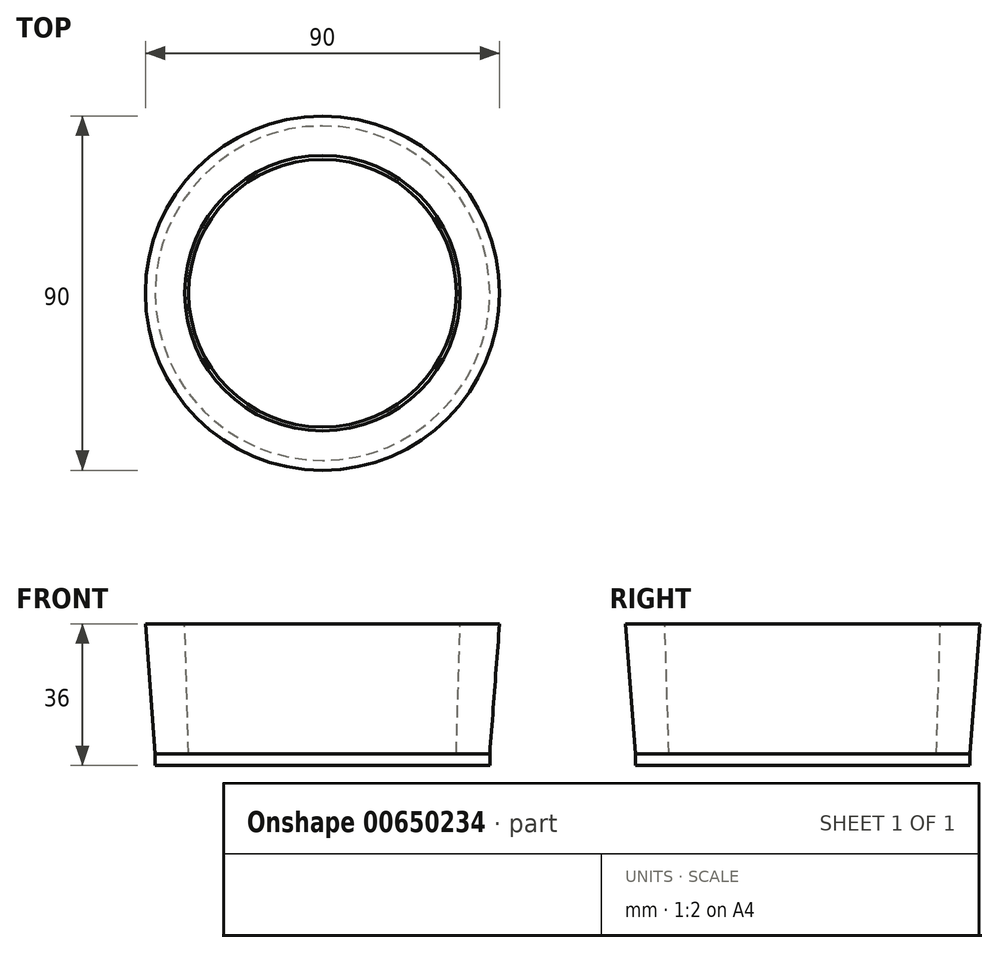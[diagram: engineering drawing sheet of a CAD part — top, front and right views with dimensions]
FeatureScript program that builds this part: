
annotation { "Feature Type Name" : "Feature", "Feature Type Description" : "" }
export const myFeature = defineFeature(function(context is Context, id is Id, definition is map)
    precondition{}
    {
        {
            var Q0;
            Q0=qCreatedBy(makeId("Right.planeOp"),FACE);
            var sketch = newSketch(context, id + "F0", { "sketchPlane" : qUnion([Q0])});
            skLineSegment(sketch, "E0", {"start": v(-45, 36) * mm, "end": v(-42.5, 3) * mm});
            skLineSegment(sketch, "E1", {"start": v(-45, 36) * mm, "end": v(-35, 36) * mm});
            skLineSegment(sketch, "E2", {"start": v(-35, 36) * mm, "end": v(-34, 3) * mm});
            skLineSegment(sketch, "E3", {"start": v(-34, 3) * mm, "end": v(-42.5, 3) * mm});
            skLineSegment(sketch, "E4", {"start": v(-34, 3) * mm, "end": v(0, 3) * mm});
            skLineSegment(sketch, "E5", {"start": v(0, 3) * mm, "end": v(0, 0) * mm});
            skLineSegment(sketch, "E6", {"start": v(0, 0) * mm, "end": v(-42.5, 0) * mm});
            skLineSegment(sketch, "E7", {"start": v(-42.5, 0) * mm, "end": v(-42.5, 3) * mm});
            skSolve(sketch);
        }
        {
            var Q0;
            Q0=makeQuery(id+"F0.imprint","IMPRINT",FACE,{"disambiguationData":[TD([[makeQuery(id+"F0.imprint","IMPRINT",EDGE,{"derivedFrom":sQuery(id+"F0.wireOp",EDGE,"E0")}),1.0]])]});
            var Q1;
            Q1=makeQuery(id+"F0.imprint","IMPRINT",FACE,{"disambiguationData":[TD([[makeQuery(id+"F0.imprint","IMPRINT",EDGE,{"derivedFrom":sQuery(id+"F0.wireOp",EDGE,"E3")}),1.0]])]});
            var Q2;
            Q2=sQuery(id+"F0.wireOp",EDGE,"E5");
            revolve(context, id + "F1", {"entities" : qUnion([Q0, Q1]), "axis" : qUnion([Q2]), "revolveType" : RevolveType.FULL});
        }
    });
